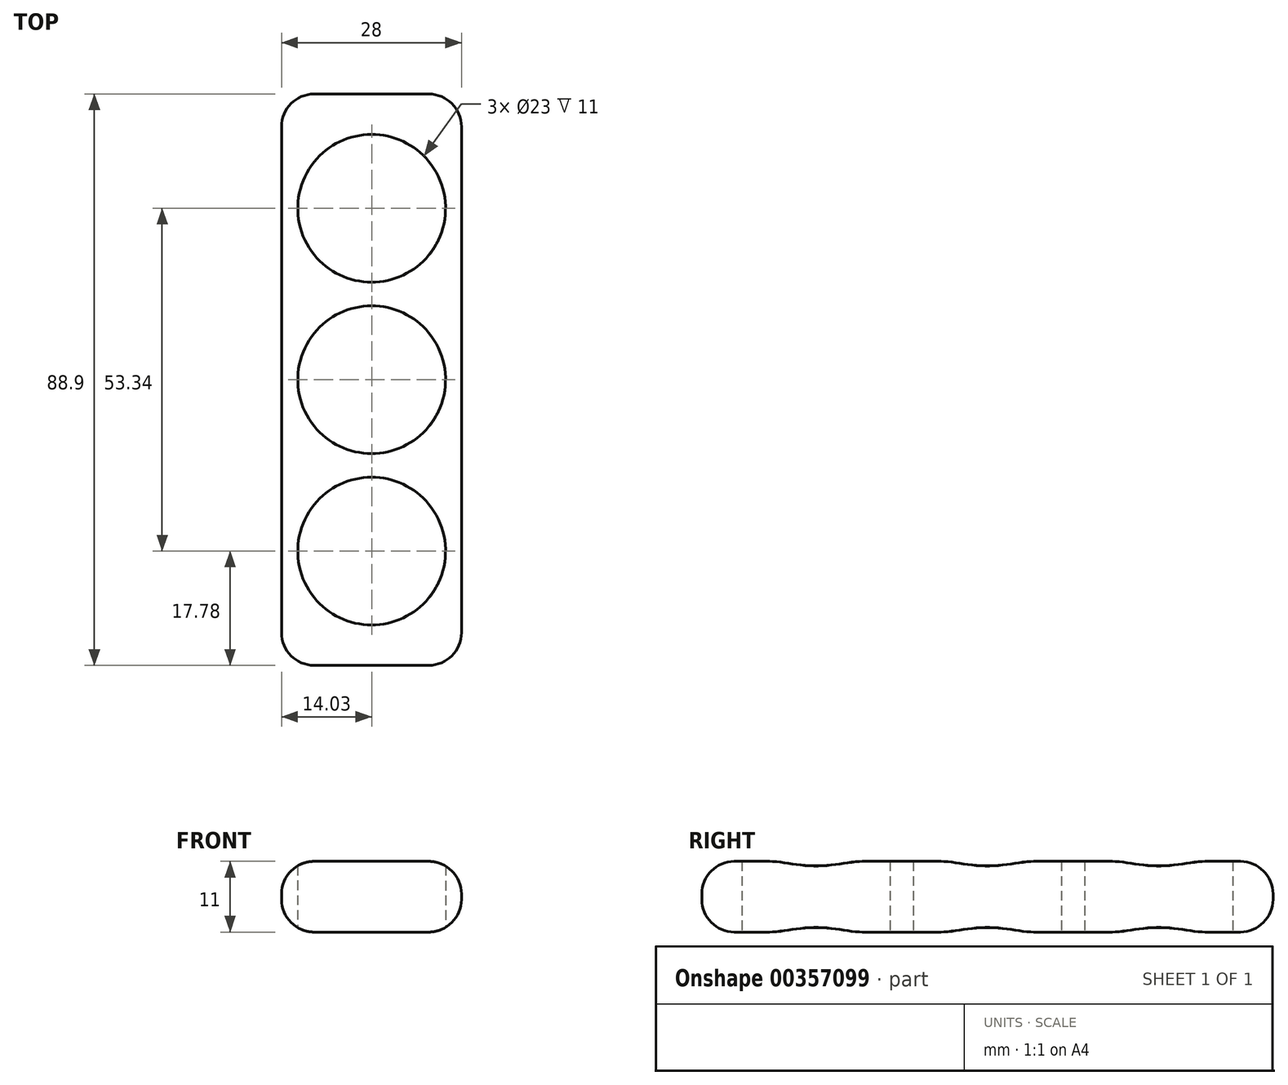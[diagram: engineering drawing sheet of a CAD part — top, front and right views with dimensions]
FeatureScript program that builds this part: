
annotation { "Feature Type Name" : "Feature", "Feature Type Description" : "" }
export const myFeature = defineFeature(function(context is Context, id is Id, definition is map)
    precondition{}
    {
        {
            var Q0;
            Q0=qCreatedBy(makeId("Top.planeOp"),FACE);
            var sketch = newSketch(context, id + "F0", { "sketchPlane" : qUnion([Q0])});
            skLineSegment(sketch, "E0.bottom", {"start": v(0, 44.45) * mm, "end": v(-28, 44.45) * mm});
            skLineSegment(sketch, "E0.top", {"start": v(0, -44.45) * mm, "end": v(-28, -44.45) * mm});
            skLineSegment(sketch, "E0.left", {"start": v(0, 44.45) * mm, "end": v(0, -44.45) * mm});
            skLineSegment(sketch, "E0.right", {"start": v(-28, 44.45) * mm, "end": v(-28, -44.45) * mm});
            skCircle(sketch, "E1", {"center": v(-13.97, 26.67) * mm, "radius": 11.5 * mm});
            skCircle(sketch, "E2", {"center": v(-13.97, 0) * mm, "radius": 11.5 * mm});
            skCircle(sketch, "E3", {"center": v(-13.97, -26.67) * mm, "radius": 11.5 * mm});
            skSolve(sketch);
        }
        {
            var Q0;
            Q0=makeQuery(id+"F0.imprint","IMPRINT",FACE,{"disambiguationData":[TD([[makeQuery(id+"F0.imprint","IMPRINT",EDGE,{"derivedFrom":sQuery(id+"F0.wireOp",EDGE,"E0.bottom")}),1.0]])]});
            extrude(context, id + "F1", {"entities" : qUnion([Q0]), "depth" : 11 * mm});
        }
        {
            var Q0;
            Q0=makeQuery(id+"F1.opExtrude","CAP_EDGE",EDGE,{"disambiguationData":[OSD([sQuery(id+"F0.wireOp",EDGE,"E0.left")])],"isStart":false});
            var Q1;
            Q1=makeQuery(id+"F1.opExtrude","CAP_EDGE",EDGE,{"disambiguationData":[OSD([sQuery(id+"F0.wireOp",EDGE,"E0.top")])],"isStart":false});
            var Q2;
            Q2=makeQuery(id+"F1.opExtrude","CAP_EDGE",EDGE,{"disambiguationData":[OSD([sQuery(id+"F0.wireOp",EDGE,"E0.top")])],"isStart":true});
            var Q3;
            Q3=makeQuery(id+"F1.opExtrude","SWEPT_EDGE",EDGE,{"disambiguationData":[OSD([sQuery(id+"F0.wireOp",EDGE,"E0.top"),sQuery(id+"F0.wireOp",EDGE,"E0.left")])]});
            var Q4;
            Q4=makeQuery(id+"F1.opExtrude","SWEPT_EDGE",EDGE,{"disambiguationData":[OSD([sQuery(id+"F0.wireOp",EDGE,"E0.top"),sQuery(id+"F0.wireOp",EDGE,"E0.right")])]});
            var Q5;
            Q5=makeQuery(id+"F1.opExtrude","CAP_EDGE",EDGE,{"disambiguationData":[OSD([sQuery(id+"F0.wireOp",EDGE,"E0.left")])],"isStart":true});
            var Q6;
            Q6=makeQuery(id+"F1.opExtrude","CAP_EDGE",EDGE,{"disambiguationData":[OSD([sQuery(id+"F0.wireOp",EDGE,"E0.right")])],"isStart":false});
            var Q7;
            Q7=makeQuery(id+"F1.opExtrude","CAP_EDGE",EDGE,{"disambiguationData":[OSD([sQuery(id+"F0.wireOp",EDGE,"E0.bottom")])],"isStart":false});
            var Q8;
            Q8=makeQuery(id+"F1.opExtrude","SWEPT_FACE",FACE,{"disambiguationData":[OSD([sQuery(id+"F0.wireOp",EDGE,"E0.right")])]});
            var Q9;
            Q9=makeQuery(id+"F1.opExtrude","CAP_EDGE",EDGE,{"disambiguationData":[OSD([sQuery(id+"F0.wireOp",EDGE,"E0.bottom")])],"isStart":true});
            var Q10;
            Q10=makeQuery(id+"F1.opExtrude","SWEPT_EDGE",EDGE,{"disambiguationData":[OSD([sQuery(id+"F0.wireOp",EDGE,"E0.bottom"),sQuery(id+"F0.wireOp",EDGE,"E0.right")])]});
            var Q11;
            Q11=makeQuery(id+"F1.opExtrude","SWEPT_EDGE",EDGE,{"disambiguationData":[OSD([sQuery(id+"F0.wireOp",EDGE,"E0.bottom"),sQuery(id+"F0.wireOp",EDGE,"E0.left")])]});
            fillet(context, id + "F2", {"entities" : qUnion([Q0, Q1, Q2, Q3, Q4, Q5, Q6, Q7, Q8, Q9, Q10, Q11]), "radius" : 5.08 * mm, "tangentPropagation" : true, "allowEdgeOverflow" : false});
        }
    });
